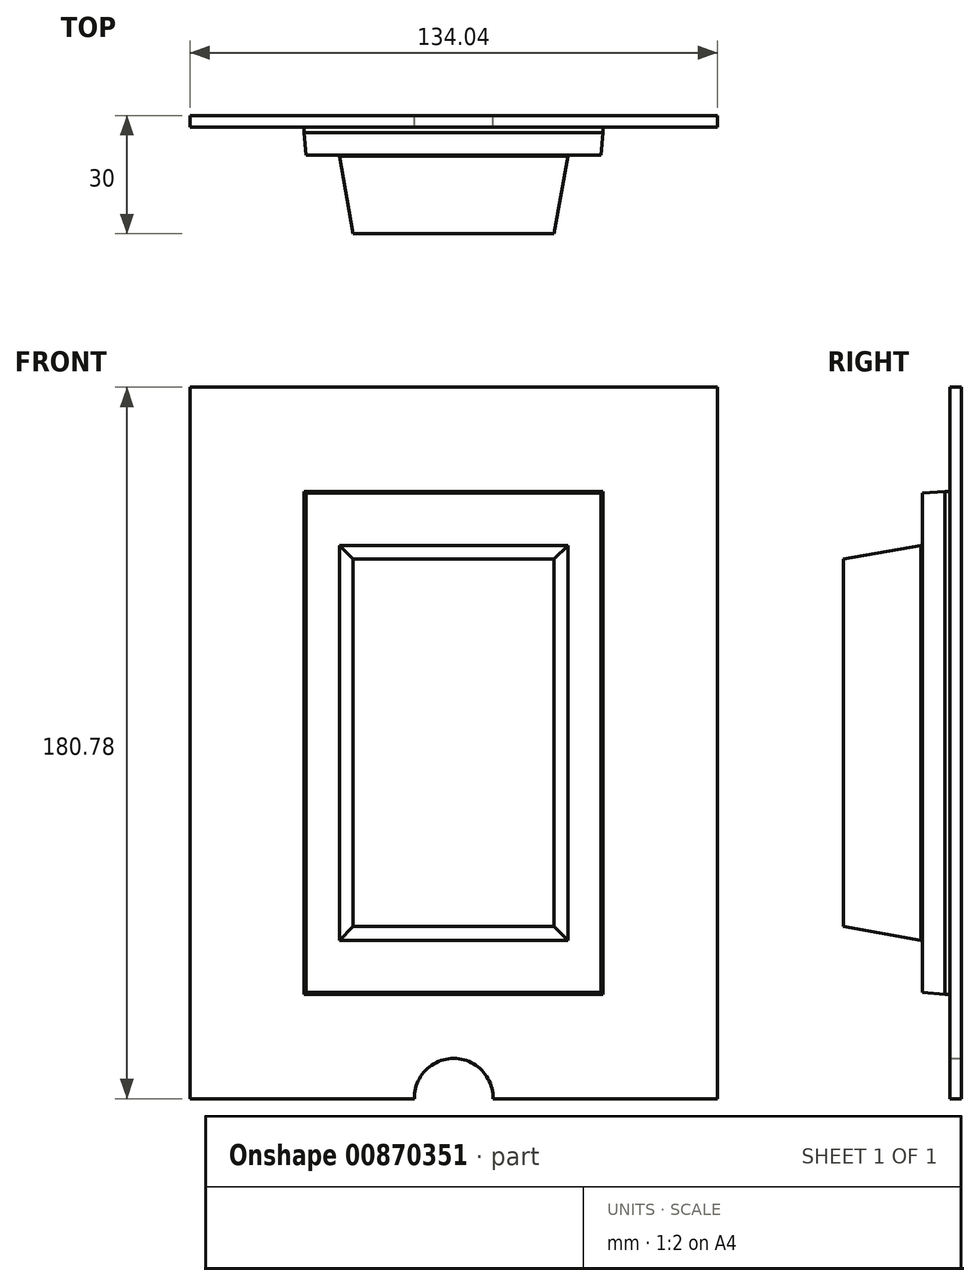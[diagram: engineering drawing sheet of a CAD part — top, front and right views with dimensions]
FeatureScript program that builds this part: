
annotation { "Feature Type Name" : "Feature", "Feature Type Description" : "" }
export const myFeature = defineFeature(function(context is Context, id is Id, definition is map)
    precondition{}
    {
        {
            var Q0;
            Q0=qCreatedBy(makeId("Front.planeOp"),FACE);
            var sketch = newSketch(context, id + "F0", { "sketchPlane" : qUnion([Q0])});
            skLineSegment(sketch, "E0.bottom", {"start": v(28.53, 49.67) * mm, "end": v(-28.53, 49.67) * mm});
            skLineSegment(sketch, "E0.top", {"start": v(28.53, -49.67) * mm, "end": v(-28.53, -49.67) * mm});
            skLineSegment(sketch, "E0.left", {"start": v(28.53, 49.67) * mm, "end": v(28.53, -49.67) * mm});
            skLineSegment(sketch, "E0.right", {"start": v(-28.53, 49.67) * mm, "end": v(-28.53, -49.67) * mm});
            skPoint(sketch, "E0.middle", {"position": v(0, 0) * mm});
            skLineSegment(sketch, "E1.bottom", {"start": v(37.98, 63.93) * mm, "end": v(-37.98, 63.93) * mm});
            skLineSegment(sketch, "E1.top", {"start": v(37.98, -63.93) * mm, "end": v(-37.98, -63.93) * mm});
            skLineSegment(sketch, "E1.left", {"start": v(37.98, 63.93) * mm, "end": v(37.98, -63.93) * mm});
            skLineSegment(sketch, "E1.right", {"start": v(-37.98, 63.93) * mm, "end": v(-37.98, -63.93) * mm});
            skLineSegment(sketch, "E2.bottom", {"start": v(67.02, 90.4) * mm, "end": v(-67.02, 90.4) * mm});
            skLineSegment(sketch, "E2.top", {"start": v(67.02, -90.4) * mm, "end": v(-67.02, -90.4) * mm});
            skLineSegment(sketch, "E2.left", {"start": v(67.02, 90.4) * mm, "end": v(67.02, -90.4) * mm});
            skLineSegment(sketch, "E2.right", {"start": v(-67.02, 90.4) * mm, "end": v(-67.02, -90.4) * mm});
            skSolve(sketch);
        }
        {
            var Q0;
            Q0=makeQuery(id+"F0.imprint","IMPRINT",FACE,{"disambiguationData":[TD([[makeQuery(id+"F0.imprint","IMPRINT",EDGE,{"derivedFrom":sQuery(id+"F0.wireOp",EDGE,"E0.bottom")}),1.0]])]});
            extrude(context, id + "F1", {"entities" : qUnion([Q0]), "depth" : 30 * mm, "offsetDistance" : 25 * mm});
        }
        {
            var Q0;
            Q0=makeQuery(id+"F0.imprint","IMPRINT",FACE,{"disambiguationData":[TD([[makeQuery(id+"F0.imprint","IMPRINT",EDGE,{"derivedFrom":sQuery(id+"F0.wireOp",EDGE,"E0.bottom")}),-1.0]])]});
            extrude(context, id + "F2", {"entities" : qUnion([Q0]), "operationType" : NewBodyOperationType.ADD, "depth" : 10 * mm, "offsetDistance" : 25 * mm});
        }
        {
            var Q0;
            Q0=makeQuery(id+"F1.opExtrude","CAP_FACE",FACE,{"disambiguationData":[OSD([sQuery(id+"F0.wireOp",EDGE,"E0.bottom"),sQuery(id+"F0.wireOp",EDGE,"E0.top"),sQuery(id+"F0.wireOp",EDGE,"E0.left"),sQuery(id+"F0.wireOp",EDGE,"E0.right")])],"isStart":false});
            chamfer(context, id + "F3", {"entities" : qUnion([Q0]), "chamferType" : ChamferType.OFFSET_ANGLE, "width" : 3 * mm, "oppositeDirection" : false, "angle" : 80 * degree, "tangentPropagation" : true});
        }
        {
            var Q0;
            Q0=makeQuery(id+"F2.opExtrude","CAP_FACE",FACE,{"disambiguationData":[OSD([sQuery(id+"F0.wireOp",EDGE,"E0.bottom"),sQuery(id+"F0.wireOp",EDGE,"E0.top"),sQuery(id+"F0.wireOp",EDGE,"E0.left"),sQuery(id+"F0.wireOp",EDGE,"E0.right"),sQuery(id+"F0.wireOp",EDGE,"E1.bottom"),sQuery(id+"F0.wireOp",EDGE,"E1.top"),sQuery(id+"F0.wireOp",EDGE,"E1.left"),sQuery(id+"F0.wireOp",EDGE,"E1.right")])],"isStart":false});
            chamfer(context, id + "F4", {"entities" : qUnion([Q0]), "chamferType" : ChamferType.OFFSET_ANGLE, "width" : 0.5 * mm, "oppositeDirection" : false, "angle" : 85 * degree, "tangentPropagation" : true});
        }
        {
            var Q0;
            Q0=makeQuery(id+"F0.imprint","IMPRINT",FACE,{"disambiguationData":[TD([[makeQuery(id+"F0.imprint","IMPRINT",EDGE,{"derivedFrom":sQuery(id+"F0.wireOp",EDGE,"E1.bottom")}),-1.0]])]});
            extrude(context, id + "F5", {"entities" : qUnion([Q0]), "operationType" : NewBodyOperationType.ADD, "depth" : 3 * mm, "offsetDistance" : 25 * mm});
        }
        {
            var Q0;
            Q0=qCreatedBy(makeId("Front.planeOp"),FACE);
            var sketch = newSketch(context, id + "F6", { "sketchPlane" : qUnion([Q0])});
            skArc(sketch, "E3", {"start": v(60.6, -90.18) * mm, "mid": v(32.28, -73.65) * mm, "end": v(0, -67.87) * mm});
            skLineSegment(sketch, "E4", {"start": v(0, -67.87) * mm, "end": v(66.6, -67.97) * mm});
            skLineSegment(sketch, "E5", {"start": v(0, 0) * mm, "end": v(0, -90.18) * mm});
            skArc(sketch, "E6.MirrorCS", {"start": v(-60.6, -90.18) * mm, "mid": v(-32.28, -73.65) * mm, "end": v(0, -67.87) * mm});
            skSolve(sketch);
        }
        {
            var Q0;
            Q0=sQuery(id+"F6.wireOp",VERTEX,"E5.end");
            var Q1;
            Q1=makeQuery(id+"F1.opExtrude","SWEPT_BODY",BODY,{"disambiguationData":[OSD([sQuery(id+"F0.wireOp",EDGE,"E0.bottom"),sQuery(id+"F0.wireOp",EDGE,"E0.top"),sQuery(id+"F0.wireOp",EDGE,"E0.left"),sQuery(id+"F0.wireOp",EDGE,"E0.right")])]});
            hole(context, id + "F7", {"style" : HoleStyle.SIMPLE, "endStyle" : HoleEndStyle.THROUGH, "oppositeDirection" : true, "holeDiameter" : 20 * mm, "majorDiameter" : 5 * mm, "isTappedThrough" : true, "tappedDepth" : 12 * mm, "tapClearance" : 3, "locations" : qUnion([Q0]), "scope" : qUnion([Q1])});
        }
    });
